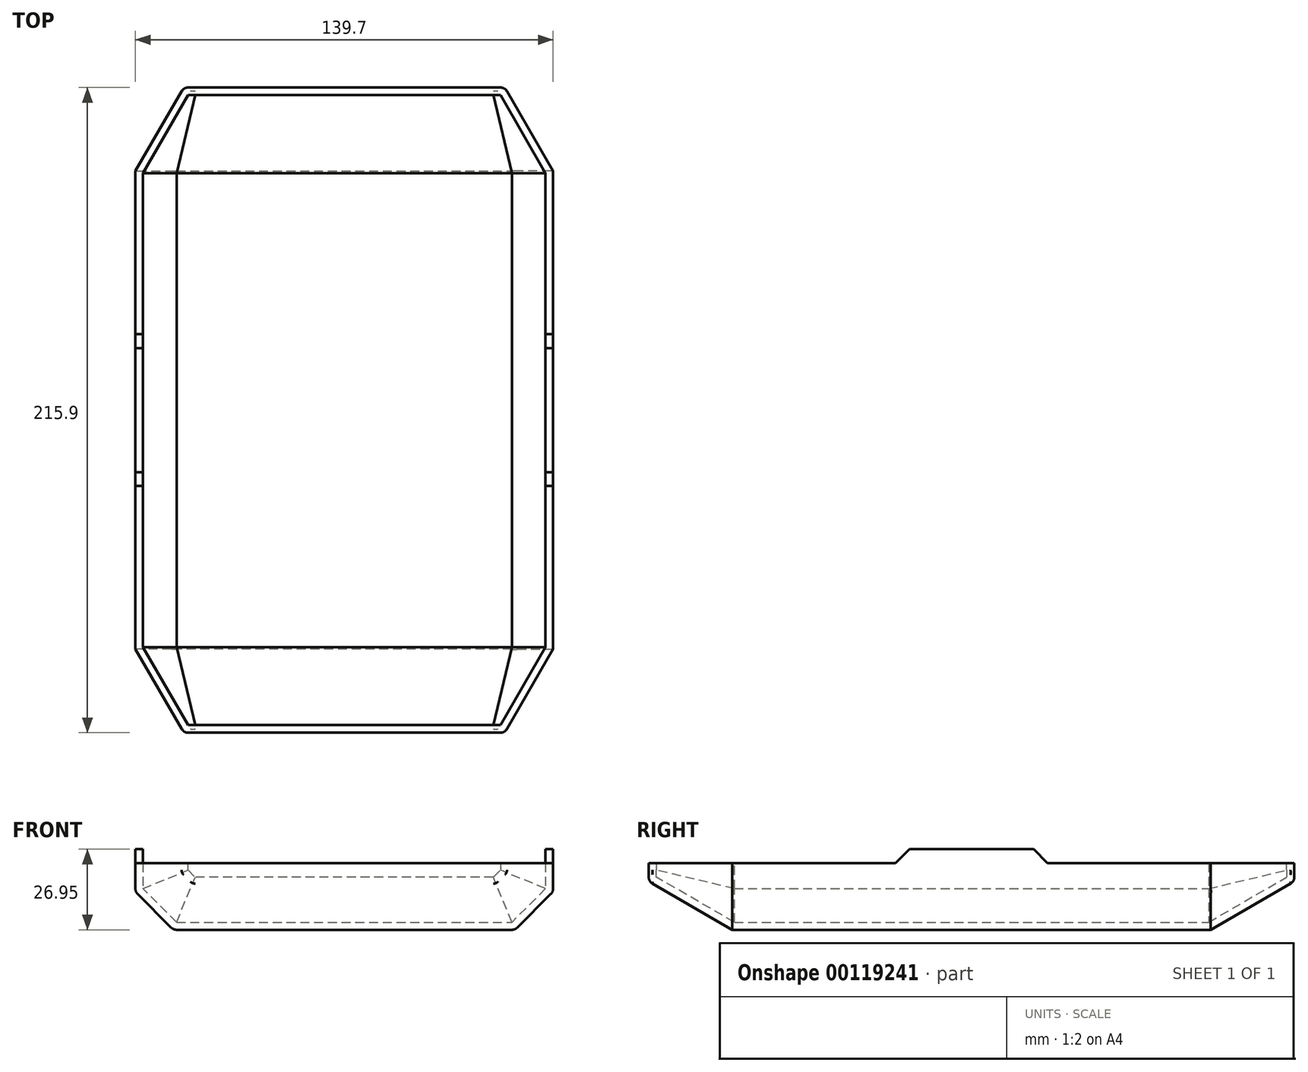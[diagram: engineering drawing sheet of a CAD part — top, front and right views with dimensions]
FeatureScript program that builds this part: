
annotation { "Feature Type Name" : "Feature", "Feature Type Description" : "" }
export const myFeature = defineFeature(function(context is Context, id is Id, definition is map)
    precondition{}
    {
        {
            var Q0;
            Q0=qCreatedBy(makeId("Right.planeOp"),FACE);
            var sketch = newSketch(context, id + "F0", { "sketchPlane" : qUnion([Q0])});
            skLineSegment(sketch, "E0", {"start": v(0, 0) * mm, "end": v(-215.9, 0) * mm});
            skLineSegment(sketch, "E1", {"start": v(-215.9, 0) * mm, "end": v(-215.9, 139.7) * mm});
            skLineSegment(sketch, "E2", {"start": v(-215.9, 139.7) * mm, "end": v(0, 139.7) * mm});
            skLineSegment(sketch, "E3", {"start": v(0, 139.7) * mm, "end": v(0, 0) * mm});
            skSolve(sketch);
        }
        {
            var Q0;
            Q0=makeQuery(id+"F0.imprint","IMPRINT",FACE,{"disambiguationData":[TD([[makeQuery(id+"F0.imprint","IMPRINT",EDGE,{"derivedFrom":sQuery(id+"F0.wireOp",EDGE,"E0")}),-1.0]])]});
            extrude(context, id + "F1", {"entities" : qUnion([Q0]), "depth" : 139.7 * mm});
        }
        {
            var Q0;
            Q0=makeQuery(id+"F1.opExtrude","CAP_EDGE",EDGE,{"disambiguationData":[OSD([sQuery(id+"F0.wireOp",EDGE,"E2")])],"isStart":true});
            var Q1;
            Q1=makeQuery(id+"F1.opExtrude","CAP_EDGE",EDGE,{"disambiguationData":[OSD([sQuery(id+"F0.wireOp",EDGE,"E0")])],"isStart":true});
            var Q2;
            Q2=makeQuery(id+"F1.opExtrude","CAP_EDGE",EDGE,{"disambiguationData":[OSD([sQuery(id+"F0.wireOp",EDGE,"E2")])],"isStart":false});
            var Q3;
            Q3=makeQuery(id+"F1.opExtrude","CAP_EDGE",EDGE,{"disambiguationData":[OSD([sQuery(id+"F0.wireOp",EDGE,"E0")])],"isStart":false});
            chamfer(context, id + "F2", {"entities" : qUnion([Q0, Q1, Q2, Q3]), "chamferType" : ChamferType.OFFSET_ANGLE, "width" : 12.7 * mm, "oppositeDirection" : false, "angle" : 45 * degree, "tangentPropagation" : true});
        }
        {
            var Q0;
            Q0=makeQuery(id+"F2.opChamfer","BLEND_EDGE",EDGE,{"blendedFrom":[makeQuery(id+"F1.opExtrude","CAP_EDGE",EDGE,{"disambiguationData":[OSD([sQuery(id+"F0.wireOp",EDGE,"E0")])],"isStart":true}),makeQuery(id+"F1.opExtrude","SWEPT_FACE",FACE,{"disambiguationData":[OSD([sQuery(id+"F0.wireOp",EDGE,"E1")])]})],"blendedInto":[makeQuery(id+"F1.opExtrude","SWEPT_FACE",FACE,{"disambiguationData":[OSD([sQuery(id+"F0.wireOp",EDGE,"E1")])]})]});
            var Q1;
            Q1=makeQuery(id+"F1.opExtrude","CAP_EDGE",EDGE,{"disambiguationData":[OSD([sQuery(id+"F0.wireOp",EDGE,"E1")])],"isStart":true});
            var Q2;
            Q2=makeQuery(id+"F2.opChamfer","BLEND_EDGE",EDGE,{"blendedFrom":[makeQuery(id+"F1.opExtrude","CAP_EDGE",EDGE,{"disambiguationData":[OSD([sQuery(id+"F0.wireOp",EDGE,"E2")])],"isStart":true}),makeQuery(id+"F1.opExtrude","SWEPT_FACE",FACE,{"disambiguationData":[OSD([sQuery(id+"F0.wireOp",EDGE,"E1")])]})],"blendedInto":[makeQuery(id+"F1.opExtrude","SWEPT_FACE",FACE,{"disambiguationData":[OSD([sQuery(id+"F0.wireOp",EDGE,"E1")])]})]});
            var Q3;
            Q3=makeQuery(id+"F1.opExtrude","SWEPT_EDGE",EDGE,{"disambiguationData":[OSD([sQuery(id+"F0.wireOp",EDGE,"E1"),sQuery(id+"F0.wireOp",EDGE,"E2")])]});
            var Q4;
            Q4=makeQuery(id+"F1.opExtrude","SWEPT_FACE",FACE,{"disambiguationData":[OSD([sQuery(id+"F0.wireOp",EDGE,"E1")])]});
            chamfer(context, id + "F3", {"entities" : qUnion([Q0, Q1, Q2, Q3, Q4]), "chamferType" : ChamferType.OFFSET_ANGLE, "width" : 27.94 * mm, "oppositeDirection" : true, "angle" : 30 * degree, "tangentPropagation" : true});
        }
        {
            var Q0;
            Q0=makeQuery(id+"F1.opExtrude","CAP_EDGE",EDGE,{"disambiguationData":[OSD([sQuery(id+"F0.wireOp",EDGE,"E3")])],"isStart":true});
            var Q1;
            Q1=makeQuery(id+"F1.opExtrude","SWEPT_EDGE",EDGE,{"disambiguationData":[OSD([sQuery(id+"F0.wireOp",EDGE,"E0"),sQuery(id+"F0.wireOp",EDGE,"E3")])]});
            var Q2;
            Q2=makeQuery(id+"F1.opExtrude","CAP_EDGE",EDGE,{"disambiguationData":[OSD([sQuery(id+"F0.wireOp",EDGE,"E3")])],"isStart":false});
            var Q3;
            Q3=makeQuery(id+"F1.opExtrude","SWEPT_EDGE",EDGE,{"disambiguationData":[OSD([sQuery(id+"F0.wireOp",EDGE,"E2"),sQuery(id+"F0.wireOp",EDGE,"E3")])]});
            var Q4;
            Q4=makeQuery(id+"F2.opChamfer","BLEND_EDGE",EDGE,{"blendedFrom":[makeQuery(id+"F1.opExtrude","CAP_EDGE",EDGE,{"disambiguationData":[OSD([sQuery(id+"F0.wireOp",EDGE,"E0")])],"isStart":false}),makeQuery(id+"F1.opExtrude","SWEPT_FACE",FACE,{"disambiguationData":[OSD([sQuery(id+"F0.wireOp",EDGE,"E3")])]})],"blendedInto":[makeQuery(id+"F1.opExtrude","SWEPT_FACE",FACE,{"disambiguationData":[OSD([sQuery(id+"F0.wireOp",EDGE,"E3")])]})]});
            var Q5;
            Q5=makeQuery(id+"F2.opChamfer","BLEND_EDGE",EDGE,{"blendedFrom":[makeQuery(id+"F1.opExtrude","CAP_EDGE",EDGE,{"disambiguationData":[OSD([sQuery(id+"F0.wireOp",EDGE,"E2")])],"isStart":false}),makeQuery(id+"F1.opExtrude","SWEPT_FACE",FACE,{"disambiguationData":[OSD([sQuery(id+"F0.wireOp",EDGE,"E3")])]})],"blendedInto":[makeQuery(id+"F1.opExtrude","SWEPT_FACE",FACE,{"disambiguationData":[OSD([sQuery(id+"F0.wireOp",EDGE,"E3")])]})]});
            var Q6;
            Q6=makeQuery(id+"F2.opChamfer","BLEND_EDGE",EDGE,{"blendedFrom":[makeQuery(id+"F1.opExtrude","CAP_EDGE",EDGE,{"disambiguationData":[OSD([sQuery(id+"F0.wireOp",EDGE,"E2")])],"isStart":true}),makeQuery(id+"F1.opExtrude","SWEPT_FACE",FACE,{"disambiguationData":[OSD([sQuery(id+"F0.wireOp",EDGE,"E3")])]})],"blendedInto":[makeQuery(id+"F1.opExtrude","SWEPT_FACE",FACE,{"disambiguationData":[OSD([sQuery(id+"F0.wireOp",EDGE,"E3")])]})]});
            var Q7;
            Q7=makeQuery(id+"F2.opChamfer","BLEND_EDGE",EDGE,{"blendedFrom":[makeQuery(id+"F1.opExtrude","CAP_EDGE",EDGE,{"disambiguationData":[OSD([sQuery(id+"F0.wireOp",EDGE,"E0")])],"isStart":true}),makeQuery(id+"F1.opExtrude","SWEPT_FACE",FACE,{"disambiguationData":[OSD([sQuery(id+"F0.wireOp",EDGE,"E3")])]})],"blendedInto":[makeQuery(id+"F1.opExtrude","SWEPT_FACE",FACE,{"disambiguationData":[OSD([sQuery(id+"F0.wireOp",EDGE,"E3")])]})]});
            chamfer(context, id + "F4", {"entities" : qUnion([Q0, Q1, Q2, Q3, Q4, Q5, Q6, Q7]), "chamferType" : ChamferType.OFFSET_ANGLE, "width" : 27.94 * mm, "oppositeDirection" : false, "angle" : 30 * degree, "tangentPropagation" : true});
        }
        {
            var Q0;
            Q0=makeQuery(id+"F1.opExtrude","SWEPT_FACE",FACE,{"disambiguationData":[OSD([sQuery(id+"F0.wireOp",EDGE,"E2")])]});
            var sketch = newSketch(context, id + "F5", { "sketchPlane" : qUnion([Q0])});
            skCircle(sketch, "E4", {"center": v(69.85, -107.95) * mm, "radius": 38.1 * mm});
            skSolve(sketch);
        }
        {
            var Q0;
            Q0=makeQuery(id+"F5.imprint","IMPRINT",FACE,{"disambiguationData":[TD([[makeQuery(id+"F5.imprint","IMPRINT",EDGE,{"derivedFrom":sQuery(id+"F5.wireOp",EDGE,"E4")}),1.0]])]});
            extrude(context, id + "F6", {"entities" : qUnion([Q0]), "operationType" : NewBodyOperationType.ADD, "depth" : 6.35 * mm});
        }
        {
            var Q0;
            {var subQ0=sQuery(id+"F0.wireOp",EDGE,"E1");Q0=makeQuery(id+"F3.opChamfer","BLEND_EDGE",EDGE,{"blendedFrom":[makeQuery(id+"F1.opExtrude","CAP_EDGE",EDGE,{"disambiguationData":[OSD([subQ0])],"isStart":false}),makeQuery(id+"F2.opChamfer","BLEND_EDGE",EDGE,{"blendedFrom":[makeQuery(id+"F1.opExtrude","CAP_EDGE",EDGE,{"disambiguationData":[OSD([sQuery(id+"F0.wireOp",EDGE,"E2")])],"isStart":false}),makeQuery(id+"F1.opExtrude","SWEPT_FACE",FACE,{"disambiguationData":[OSD([subQ0])]})],"blendedInto":[makeQuery(id+"F1.opExtrude","SWEPT_FACE",FACE,{"disambiguationData":[OSD([subQ0])]})]})],"blendedInto":[]});}
            var Q1;
            {var subQ0=sQuery(id+"F0.wireOp",EDGE,"E1");var subQ1=sQuery(id+"F0.wireOp",EDGE,"E2");Q1=makeQuery(id+"F3.opChamfer","BLEND_EDGE",EDGE,{"blendedFrom":[makeQuery(id+"F1.opExtrude","SWEPT_EDGE",EDGE,{"disambiguationData":[OSD([subQ0,subQ1])]}),makeQuery(id+"F2.opChamfer","BLEND_EDGE",EDGE,{"blendedFrom":[makeQuery(id+"F1.opExtrude","CAP_EDGE",EDGE,{"disambiguationData":[OSD([subQ1])],"isStart":false}),makeQuery(id+"F1.opExtrude","SWEPT_FACE",FACE,{"disambiguationData":[OSD([subQ0])]})],"blendedInto":[makeQuery(id+"F1.opExtrude","SWEPT_FACE",FACE,{"disambiguationData":[OSD([subQ0])]})]})],"blendedInto":[]});}
            var Q2;
            {var subQ0=sQuery(id+"F0.wireOp",EDGE,"E2");Q2=makeQuery(id+"F2.opChamfer","BLEND_EDGE",EDGE,{"blendedFrom":[makeQuery(id+"F1.opExtrude","CAP_EDGE",EDGE,{"disambiguationData":[OSD([subQ0])],"isStart":false}),makeQuery(id+"F1.opExtrude","SWEPT_FACE",FACE,{"disambiguationData":[OSD([subQ0])]})],"blendedInto":[makeQuery(id+"F1.opExtrude","SWEPT_FACE",FACE,{"disambiguationData":[OSD([subQ0])]})]});}
            var Q3;
            {var subQ0=sQuery(id+"F0.wireOp",EDGE,"E2");Q3=makeQuery(id+"F2.opChamfer","BLEND_EDGE",EDGE,{"blendedFrom":[makeQuery(id+"F1.opExtrude","CAP_EDGE",EDGE,{"disambiguationData":[OSD([subQ0])],"isStart":false}),makeQuery(id+"F1.opExtrude","CAP_FACE",FACE,{"disambiguationData":[OSD([sQuery(id+"F0.wireOp",EDGE,"E0"),sQuery(id+"F0.wireOp",EDGE,"E1"),subQ0,sQuery(id+"F0.wireOp",EDGE,"E3")])],"isStart":false})],"blendedInto":[makeQuery(id+"F1.opExtrude","CAP_FACE",FACE,{"disambiguationData":[OSD([sQuery(id+"F0.wireOp",EDGE,"E0"),sQuery(id+"F0.wireOp",EDGE,"E1"),subQ0,sQuery(id+"F0.wireOp",EDGE,"E3")])],"isStart":false})]});}
            var Q4;
            {var subQ0=makeQuery(id+"F1.opExtrude","SWEPT_FACE",FACE,{"disambiguationData":[OSD([sQuery(id+"F0.wireOp",EDGE,"E1")])]});Q4=makeQuery(id+"F3.opChamfer","BLEND_EDGE",EDGE,{"blendedFrom":[makeQuery(id+"F2.opChamfer","BLEND_EDGE",EDGE,{"blendedFrom":[makeQuery(id+"F1.opExtrude","CAP_EDGE",EDGE,{"disambiguationData":[OSD([sQuery(id+"F0.wireOp",EDGE,"E2")])],"isStart":false}),subQ0],"blendedInto":[subQ0]}),subQ0],"blendedInto":[subQ0]});}
            var Q5;
            {var subQ0=sQuery(id+"F0.wireOp",EDGE,"E1");Q5=makeQuery(id+"F3.opChamfer","BLEND_EDGE",EDGE,{"blendedFrom":[makeQuery(id+"F1.opExtrude","SWEPT_EDGE",EDGE,{"disambiguationData":[OSD([subQ0,sQuery(id+"F0.wireOp",EDGE,"E2")])]}),makeQuery(id+"F1.opExtrude","SWEPT_FACE",FACE,{"disambiguationData":[OSD([subQ0])]})],"blendedInto":[makeQuery(id+"F1.opExtrude","SWEPT_FACE",FACE,{"disambiguationData":[OSD([subQ0])]})]});}
            var Q6;
            {var subQ0=sQuery(id+"F0.wireOp",EDGE,"E1");Q6=makeQuery(id+"F3.opChamfer","BLEND_EDGE",EDGE,{"blendedFrom":[makeQuery(id+"F1.opExtrude","CAP_EDGE",EDGE,{"disambiguationData":[OSD([subQ0])],"isStart":false}),makeQuery(id+"F1.opExtrude","SWEPT_FACE",FACE,{"disambiguationData":[OSD([subQ0])]})],"blendedInto":[makeQuery(id+"F1.opExtrude","SWEPT_FACE",FACE,{"disambiguationData":[OSD([subQ0])]})]});}
            var Q7;
            {var subQ0=sQuery(id+"F0.wireOp",EDGE,"E3");var subQ1=sQuery(id+"F0.wireOp",EDGE,"E2");Q7=makeQuery(id+"F4.opChamfer","BLEND_EDGE",EDGE,{"blendedFrom":[makeQuery(id+"F1.opExtrude","SWEPT_EDGE",EDGE,{"disambiguationData":[OSD([subQ1,subQ0])]}),makeQuery(id+"F2.opChamfer","BLEND_EDGE",EDGE,{"blendedFrom":[makeQuery(id+"F1.opExtrude","CAP_EDGE",EDGE,{"disambiguationData":[OSD([subQ1])],"isStart":false}),makeQuery(id+"F1.opExtrude","SWEPT_FACE",FACE,{"disambiguationData":[OSD([subQ0])]})],"blendedInto":[makeQuery(id+"F1.opExtrude","SWEPT_FACE",FACE,{"disambiguationData":[OSD([subQ0])]})]})],"blendedInto":[]});}
            var Q8;
            {var subQ0=sQuery(id+"F0.wireOp",EDGE,"E3");Q8=makeQuery(id+"F4.opChamfer","BLEND_EDGE",EDGE,{"blendedFrom":[makeQuery(id+"F2.opChamfer","BLEND_EDGE",EDGE,{"blendedFrom":[makeQuery(id+"F1.opExtrude","CAP_EDGE",EDGE,{"disambiguationData":[OSD([sQuery(id+"F0.wireOp",EDGE,"E2")])],"isStart":false}),makeQuery(id+"F1.opExtrude","SWEPT_FACE",FACE,{"disambiguationData":[OSD([subQ0])]})],"blendedInto":[makeQuery(id+"F1.opExtrude","SWEPT_FACE",FACE,{"disambiguationData":[OSD([subQ0])]})]}),makeQuery(id+"F1.opExtrude","CAP_EDGE",EDGE,{"disambiguationData":[OSD([subQ0])],"isStart":false})],"blendedInto":[]});}
            var Q9;
            {var subQ0=makeQuery(id+"F1.opExtrude","SWEPT_FACE",FACE,{"disambiguationData":[OSD([sQuery(id+"F0.wireOp",EDGE,"E3")])]});Q9=makeQuery(id+"F4.opChamfer","BLEND_EDGE",EDGE,{"blendedFrom":[makeQuery(id+"F2.opChamfer","BLEND_EDGE",EDGE,{"blendedFrom":[makeQuery(id+"F1.opExtrude","CAP_EDGE",EDGE,{"disambiguationData":[OSD([sQuery(id+"F0.wireOp",EDGE,"E2")])],"isStart":false}),subQ0],"blendedInto":[subQ0]}),subQ0],"blendedInto":[subQ0]});}
            var Q10;
            {var subQ0=sQuery(id+"F0.wireOp",EDGE,"E3");Q10=makeQuery(id+"F4.opChamfer","BLEND_EDGE",EDGE,{"blendedFrom":[makeQuery(id+"F1.opExtrude","CAP_EDGE",EDGE,{"disambiguationData":[OSD([subQ0])],"isStart":false}),makeQuery(id+"F1.opExtrude","SWEPT_FACE",FACE,{"disambiguationData":[OSD([subQ0])]})],"blendedInto":[makeQuery(id+"F1.opExtrude","SWEPT_FACE",FACE,{"disambiguationData":[OSD([subQ0])]})]});}
            var Q11;
            {var subQ0=sQuery(id+"F0.wireOp",EDGE,"E1");Q11=makeQuery(id+"F3.opChamfer","BLEND_EDGE",EDGE,{"blendedFrom":[makeQuery(id+"F2.opChamfer","BLEND_EDGE",EDGE,{"blendedFrom":[makeQuery(id+"F1.opExtrude","CAP_EDGE",EDGE,{"disambiguationData":[OSD([sQuery(id+"F0.wireOp",EDGE,"E0")])],"isStart":false}),makeQuery(id+"F1.opExtrude","SWEPT_FACE",FACE,{"disambiguationData":[OSD([subQ0])]})],"blendedInto":[makeQuery(id+"F1.opExtrude","SWEPT_FACE",FACE,{"disambiguationData":[OSD([subQ0])]})]}),makeQuery(id+"F1.opExtrude","CAP_EDGE",EDGE,{"disambiguationData":[OSD([subQ0])],"isStart":false})],"blendedInto":[]});}
            var Q12;
            {var subQ0=sQuery(id+"F0.wireOp",EDGE,"E1");var subQ1=sQuery(id+"F0.wireOp",EDGE,"E0");Q12=makeQuery(id+"F3.opChamfer","BLEND_EDGE",EDGE,{"blendedFrom":[makeQuery(id+"F1.opExtrude","SWEPT_EDGE",EDGE,{"disambiguationData":[OSD([subQ1,subQ0])]}),makeQuery(id+"F2.opChamfer","BLEND_EDGE",EDGE,{"blendedFrom":[makeQuery(id+"F1.opExtrude","CAP_EDGE",EDGE,{"disambiguationData":[OSD([subQ1])],"isStart":false}),makeQuery(id+"F1.opExtrude","SWEPT_FACE",FACE,{"disambiguationData":[OSD([subQ0])]})],"blendedInto":[makeQuery(id+"F1.opExtrude","SWEPT_FACE",FACE,{"disambiguationData":[OSD([subQ0])]})]})],"blendedInto":[]});}
            var Q13;
            {var subQ0=makeQuery(id+"F1.opExtrude","SWEPT_FACE",FACE,{"disambiguationData":[OSD([sQuery(id+"F0.wireOp",EDGE,"E1")])]});Q13=makeQuery(id+"F3.opChamfer","BLEND_EDGE",EDGE,{"blendedFrom":[makeQuery(id+"F2.opChamfer","BLEND_EDGE",EDGE,{"blendedFrom":[makeQuery(id+"F1.opExtrude","CAP_EDGE",EDGE,{"disambiguationData":[OSD([sQuery(id+"F0.wireOp",EDGE,"E0")])],"isStart":false}),subQ0],"blendedInto":[subQ0]}),subQ0],"blendedInto":[subQ0]});}
            var Q14;
            {var subQ0=sQuery(id+"F0.wireOp",EDGE,"E1");Q14=makeQuery(id+"F3.opChamfer","BLEND_EDGE",EDGE,{"blendedFrom":[makeQuery(id+"F1.opExtrude","SWEPT_EDGE",EDGE,{"disambiguationData":[OSD([sQuery(id+"F0.wireOp",EDGE,"E0"),subQ0])]}),makeQuery(id+"F1.opExtrude","SWEPT_FACE",FACE,{"disambiguationData":[OSD([subQ0])]})],"blendedInto":[makeQuery(id+"F1.opExtrude","SWEPT_FACE",FACE,{"disambiguationData":[OSD([subQ0])]})]});}
            var Q15;
            {var subQ0=sQuery(id+"F0.wireOp",EDGE,"E1");var subQ1=sQuery(id+"F0.wireOp",EDGE,"E0");Q15=makeQuery(id+"F3.opChamfer","BLEND_EDGE",EDGE,{"blendedFrom":[makeQuery(id+"F1.opExtrude","SWEPT_EDGE",EDGE,{"disambiguationData":[OSD([subQ1,subQ0])]}),makeQuery(id+"F2.opChamfer","BLEND_EDGE",EDGE,{"blendedFrom":[makeQuery(id+"F1.opExtrude","CAP_EDGE",EDGE,{"disambiguationData":[OSD([subQ1])],"isStart":true}),makeQuery(id+"F1.opExtrude","SWEPT_FACE",FACE,{"disambiguationData":[OSD([subQ0])]})],"blendedInto":[makeQuery(id+"F1.opExtrude","SWEPT_FACE",FACE,{"disambiguationData":[OSD([subQ0])]})]})],"blendedInto":[]});}
            var Q16;
            {var subQ0=sQuery(id+"F0.wireOp",EDGE,"E1");Q16=makeQuery(id+"F3.opChamfer","BLEND_EDGE",EDGE,{"blendedFrom":[makeQuery(id+"F1.opExtrude","CAP_EDGE",EDGE,{"disambiguationData":[OSD([subQ0])],"isStart":true}),makeQuery(id+"F1.opExtrude","SWEPT_FACE",FACE,{"disambiguationData":[OSD([subQ0])]})],"blendedInto":[makeQuery(id+"F1.opExtrude","SWEPT_FACE",FACE,{"disambiguationData":[OSD([subQ0])]})]});}
            var Q17;
            {var subQ0=makeQuery(id+"F1.opExtrude","SWEPT_FACE",FACE,{"disambiguationData":[OSD([sQuery(id+"F0.wireOp",EDGE,"E1")])]});Q17=makeQuery(id+"F3.opChamfer","BLEND_EDGE",EDGE,{"blendedFrom":[makeQuery(id+"F2.opChamfer","BLEND_EDGE",EDGE,{"blendedFrom":[makeQuery(id+"F1.opExtrude","CAP_EDGE",EDGE,{"disambiguationData":[OSD([sQuery(id+"F0.wireOp",EDGE,"E0")])],"isStart":true}),subQ0],"blendedInto":[subQ0]}),subQ0],"blendedInto":[subQ0]});}
            var Q18;
            {var subQ0=makeQuery(id+"F1.opExtrude","SWEPT_FACE",FACE,{"disambiguationData":[OSD([sQuery(id+"F0.wireOp",EDGE,"E1")])]});Q18=makeQuery(id+"F3.opChamfer","BLEND_EDGE",EDGE,{"blendedFrom":[makeQuery(id+"F2.opChamfer","BLEND_EDGE",EDGE,{"blendedFrom":[makeQuery(id+"F1.opExtrude","CAP_EDGE",EDGE,{"disambiguationData":[OSD([sQuery(id+"F0.wireOp",EDGE,"E2")])],"isStart":true}),subQ0],"blendedInto":[subQ0]}),subQ0],"blendedInto":[subQ0]});}
            var Q19;
            {var subQ0=sQuery(id+"F0.wireOp",EDGE,"E1");var subQ1=sQuery(id+"F0.wireOp",EDGE,"E2");Q19=makeQuery(id+"F3.opChamfer","BLEND_EDGE",EDGE,{"blendedFrom":[makeQuery(id+"F1.opExtrude","SWEPT_EDGE",EDGE,{"disambiguationData":[OSD([subQ0,subQ1])]}),makeQuery(id+"F2.opChamfer","BLEND_EDGE",EDGE,{"blendedFrom":[makeQuery(id+"F1.opExtrude","CAP_EDGE",EDGE,{"disambiguationData":[OSD([subQ1])],"isStart":true}),makeQuery(id+"F1.opExtrude","SWEPT_FACE",FACE,{"disambiguationData":[OSD([subQ0])]})],"blendedInto":[makeQuery(id+"F1.opExtrude","SWEPT_FACE",FACE,{"disambiguationData":[OSD([subQ0])]})]})],"blendedInto":[]});}
            var Q20;
            {var subQ0=sQuery(id+"F0.wireOp",EDGE,"E1");Q20=makeQuery(id+"F3.opChamfer","BLEND_EDGE",EDGE,{"blendedFrom":[makeQuery(id+"F1.opExtrude","CAP_EDGE",EDGE,{"disambiguationData":[OSD([subQ0])],"isStart":true}),makeQuery(id+"F2.opChamfer","BLEND_EDGE",EDGE,{"blendedFrom":[makeQuery(id+"F1.opExtrude","CAP_EDGE",EDGE,{"disambiguationData":[OSD([sQuery(id+"F0.wireOp",EDGE,"E2")])],"isStart":true}),makeQuery(id+"F1.opExtrude","SWEPT_FACE",FACE,{"disambiguationData":[OSD([subQ0])]})],"blendedInto":[makeQuery(id+"F1.opExtrude","SWEPT_FACE",FACE,{"disambiguationData":[OSD([subQ0])]})]})],"blendedInto":[]});}
            var Q21;
            {var subQ0=sQuery(id+"F0.wireOp",EDGE,"E1");Q21=makeQuery(id+"F3.opChamfer","BLEND_EDGE",EDGE,{"blendedFrom":[makeQuery(id+"F2.opChamfer","BLEND_EDGE",EDGE,{"blendedFrom":[makeQuery(id+"F1.opExtrude","CAP_EDGE",EDGE,{"disambiguationData":[OSD([sQuery(id+"F0.wireOp",EDGE,"E0")])],"isStart":true}),makeQuery(id+"F1.opExtrude","SWEPT_FACE",FACE,{"disambiguationData":[OSD([subQ0])]})],"blendedInto":[makeQuery(id+"F1.opExtrude","SWEPT_FACE",FACE,{"disambiguationData":[OSD([subQ0])]})]}),makeQuery(id+"F1.opExtrude","CAP_EDGE",EDGE,{"disambiguationData":[OSD([subQ0])],"isStart":true})],"blendedInto":[]});}
            var Q22;
            {var subQ0=sQuery(id+"F0.wireOp",EDGE,"E0");Q22=makeQuery(id+"F2.opChamfer","BLEND_EDGE",EDGE,{"blendedFrom":[makeQuery(id+"F1.opExtrude","CAP_EDGE",EDGE,{"disambiguationData":[OSD([subQ0])],"isStart":true}),makeQuery(id+"F1.opExtrude","CAP_FACE",FACE,{"disambiguationData":[OSD([subQ0,sQuery(id+"F0.wireOp",EDGE,"E1"),sQuery(id+"F0.wireOp",EDGE,"E2"),sQuery(id+"F0.wireOp",EDGE,"E3")])],"isStart":true})],"blendedInto":[makeQuery(id+"F1.opExtrude","CAP_FACE",FACE,{"disambiguationData":[OSD([subQ0,sQuery(id+"F0.wireOp",EDGE,"E1"),sQuery(id+"F0.wireOp",EDGE,"E2"),sQuery(id+"F0.wireOp",EDGE,"E3")])],"isStart":true})]});}
            var Q23;
            {var subQ0=sQuery(id+"F0.wireOp",EDGE,"E2");Q23=makeQuery(id+"F2.opChamfer","BLEND_EDGE",EDGE,{"blendedFrom":[makeQuery(id+"F1.opExtrude","CAP_EDGE",EDGE,{"disambiguationData":[OSD([subQ0])],"isStart":true}),makeQuery(id+"F1.opExtrude","SWEPT_FACE",FACE,{"disambiguationData":[OSD([subQ0])]})],"blendedInto":[makeQuery(id+"F1.opExtrude","SWEPT_FACE",FACE,{"disambiguationData":[OSD([subQ0])]})]});}
            var Q24;
            {var subQ0=sQuery(id+"F0.wireOp",EDGE,"E2");Q24=makeQuery(id+"F2.opChamfer","BLEND_EDGE",EDGE,{"blendedFrom":[makeQuery(id+"F1.opExtrude","CAP_EDGE",EDGE,{"disambiguationData":[OSD([subQ0])],"isStart":true}),makeQuery(id+"F1.opExtrude","CAP_FACE",FACE,{"disambiguationData":[OSD([sQuery(id+"F0.wireOp",EDGE,"E0"),sQuery(id+"F0.wireOp",EDGE,"E1"),subQ0,sQuery(id+"F0.wireOp",EDGE,"E3")])],"isStart":true})],"blendedInto":[makeQuery(id+"F1.opExtrude","CAP_FACE",FACE,{"disambiguationData":[OSD([sQuery(id+"F0.wireOp",EDGE,"E0"),sQuery(id+"F0.wireOp",EDGE,"E1"),subQ0,sQuery(id+"F0.wireOp",EDGE,"E3")])],"isStart":true})]});}
            var Q25;
            {var subQ0=sQuery(id+"F0.wireOp",EDGE,"E3");var subQ1=sQuery(id+"F0.wireOp",EDGE,"E2");Q25=makeQuery(id+"F4.opChamfer","BLEND_EDGE",EDGE,{"blendedFrom":[makeQuery(id+"F1.opExtrude","SWEPT_EDGE",EDGE,{"disambiguationData":[OSD([subQ1,subQ0])]}),makeQuery(id+"F2.opChamfer","BLEND_EDGE",EDGE,{"blendedFrom":[makeQuery(id+"F1.opExtrude","CAP_EDGE",EDGE,{"disambiguationData":[OSD([subQ1])],"isStart":true}),makeQuery(id+"F1.opExtrude","SWEPT_FACE",FACE,{"disambiguationData":[OSD([subQ0])]})],"blendedInto":[makeQuery(id+"F1.opExtrude","SWEPT_FACE",FACE,{"disambiguationData":[OSD([subQ0])]})]})],"blendedInto":[]});}
            var Q26;
            {var subQ0=sQuery(id+"F0.wireOp",EDGE,"E3");Q26=makeQuery(id+"F4.opChamfer","BLEND_EDGE",EDGE,{"blendedFrom":[makeQuery(id+"F2.opChamfer","BLEND_EDGE",EDGE,{"blendedFrom":[makeQuery(id+"F1.opExtrude","CAP_EDGE",EDGE,{"disambiguationData":[OSD([sQuery(id+"F0.wireOp",EDGE,"E2")])],"isStart":true}),makeQuery(id+"F1.opExtrude","SWEPT_FACE",FACE,{"disambiguationData":[OSD([subQ0])]})],"blendedInto":[makeQuery(id+"F1.opExtrude","SWEPT_FACE",FACE,{"disambiguationData":[OSD([subQ0])]})]}),makeQuery(id+"F1.opExtrude","CAP_EDGE",EDGE,{"disambiguationData":[OSD([subQ0])],"isStart":true})],"blendedInto":[]});}
            var Q27;
            {var subQ0=makeQuery(id+"F1.opExtrude","SWEPT_FACE",FACE,{"disambiguationData":[OSD([sQuery(id+"F0.wireOp",EDGE,"E3")])]});Q27=makeQuery(id+"F4.opChamfer","BLEND_EDGE",EDGE,{"blendedFrom":[makeQuery(id+"F2.opChamfer","BLEND_EDGE",EDGE,{"blendedFrom":[makeQuery(id+"F1.opExtrude","CAP_EDGE",EDGE,{"disambiguationData":[OSD([sQuery(id+"F0.wireOp",EDGE,"E2")])],"isStart":true}),subQ0],"blendedInto":[subQ0]}),subQ0],"blendedInto":[subQ0]});}
            var Q28;
            {var subQ0=sQuery(id+"F0.wireOp",EDGE,"E3");Q28=makeQuery(id+"F4.opChamfer","BLEND_EDGE",EDGE,{"blendedFrom":[makeQuery(id+"F1.opExtrude","SWEPT_EDGE",EDGE,{"disambiguationData":[OSD([sQuery(id+"F0.wireOp",EDGE,"E2"),subQ0])]}),makeQuery(id+"F1.opExtrude","SWEPT_FACE",FACE,{"disambiguationData":[OSD([subQ0])]})],"blendedInto":[makeQuery(id+"F1.opExtrude","SWEPT_FACE",FACE,{"disambiguationData":[OSD([subQ0])]})]});}
            var Q29;
            {var subQ0=sQuery(id+"F0.wireOp",EDGE,"E3");Q29=makeQuery(id+"F4.opChamfer","BLEND_EDGE",EDGE,{"blendedFrom":[makeQuery(id+"F1.opExtrude","CAP_EDGE",EDGE,{"disambiguationData":[OSD([subQ0])],"isStart":true}),makeQuery(id+"F1.opExtrude","SWEPT_FACE",FACE,{"disambiguationData":[OSD([subQ0])]})],"blendedInto":[makeQuery(id+"F1.opExtrude","SWEPT_FACE",FACE,{"disambiguationData":[OSD([subQ0])]})]});}
            var Q30;
            {var subQ0=sQuery(id+"F0.wireOp",EDGE,"E3");Q30=makeQuery(id+"F4.opChamfer","BLEND_EDGE",EDGE,{"blendedFrom":[makeQuery(id+"F2.opChamfer","BLEND_EDGE",EDGE,{"blendedFrom":[makeQuery(id+"F1.opExtrude","CAP_EDGE",EDGE,{"disambiguationData":[OSD([sQuery(id+"F0.wireOp",EDGE,"E0")])],"isStart":true}),makeQuery(id+"F1.opExtrude","SWEPT_FACE",FACE,{"disambiguationData":[OSD([subQ0])]})],"blendedInto":[makeQuery(id+"F1.opExtrude","SWEPT_FACE",FACE,{"disambiguationData":[OSD([subQ0])]})]}),makeQuery(id+"F1.opExtrude","CAP_EDGE",EDGE,{"disambiguationData":[OSD([subQ0])],"isStart":true})],"blendedInto":[]});}
            var Q31;
            {var subQ0=sQuery(id+"F0.wireOp",EDGE,"E3");var subQ1=sQuery(id+"F0.wireOp",EDGE,"E0");Q31=makeQuery(id+"F4.opChamfer","BLEND_EDGE",EDGE,{"blendedFrom":[makeQuery(id+"F1.opExtrude","SWEPT_EDGE",EDGE,{"disambiguationData":[OSD([subQ1,subQ0])]}),makeQuery(id+"F2.opChamfer","BLEND_EDGE",EDGE,{"blendedFrom":[makeQuery(id+"F1.opExtrude","CAP_EDGE",EDGE,{"disambiguationData":[OSD([subQ1])],"isStart":true}),makeQuery(id+"F1.opExtrude","SWEPT_FACE",FACE,{"disambiguationData":[OSD([subQ0])]})],"blendedInto":[makeQuery(id+"F1.opExtrude","SWEPT_FACE",FACE,{"disambiguationData":[OSD([subQ0])]})]})],"blendedInto":[]});}
            var Q32;
            {var subQ0=makeQuery(id+"F1.opExtrude","SWEPT_FACE",FACE,{"disambiguationData":[OSD([sQuery(id+"F0.wireOp",EDGE,"E3")])]});Q32=makeQuery(id+"F4.opChamfer","BLEND_EDGE",EDGE,{"blendedFrom":[makeQuery(id+"F2.opChamfer","BLEND_EDGE",EDGE,{"blendedFrom":[makeQuery(id+"F1.opExtrude","CAP_EDGE",EDGE,{"disambiguationData":[OSD([sQuery(id+"F0.wireOp",EDGE,"E0")])],"isStart":true}),subQ0],"blendedInto":[subQ0]}),subQ0],"blendedInto":[subQ0]});}
            var Q33;
            {var subQ0=sQuery(id+"F0.wireOp",EDGE,"E3");Q33=makeQuery(id+"F4.opChamfer","BLEND_EDGE",EDGE,{"blendedFrom":[makeQuery(id+"F1.opExtrude","SWEPT_EDGE",EDGE,{"disambiguationData":[OSD([sQuery(id+"F0.wireOp",EDGE,"E0"),subQ0])]}),makeQuery(id+"F1.opExtrude","SWEPT_FACE",FACE,{"disambiguationData":[OSD([subQ0])]})],"blendedInto":[makeQuery(id+"F1.opExtrude","SWEPT_FACE",FACE,{"disambiguationData":[OSD([subQ0])]})]});}
            var Q34;
            {var subQ0=makeQuery(id+"F1.opExtrude","SWEPT_FACE",FACE,{"disambiguationData":[OSD([sQuery(id+"F0.wireOp",EDGE,"E3")])]});Q34=makeQuery(id+"F4.opChamfer","BLEND_EDGE",EDGE,{"blendedFrom":[makeQuery(id+"F2.opChamfer","BLEND_EDGE",EDGE,{"blendedFrom":[makeQuery(id+"F1.opExtrude","CAP_EDGE",EDGE,{"disambiguationData":[OSD([sQuery(id+"F0.wireOp",EDGE,"E0")])],"isStart":false}),subQ0],"blendedInto":[subQ0]}),subQ0],"blendedInto":[subQ0]});}
            var Q35;
            {var subQ0=sQuery(id+"F0.wireOp",EDGE,"E3");Q35=makeQuery(id+"F4.opChamfer","BLEND_EDGE",EDGE,{"blendedFrom":[makeQuery(id+"F2.opChamfer","BLEND_EDGE",EDGE,{"blendedFrom":[makeQuery(id+"F1.opExtrude","CAP_EDGE",EDGE,{"disambiguationData":[OSD([sQuery(id+"F0.wireOp",EDGE,"E0")])],"isStart":false}),makeQuery(id+"F1.opExtrude","SWEPT_FACE",FACE,{"disambiguationData":[OSD([subQ0])]})],"blendedInto":[makeQuery(id+"F1.opExtrude","SWEPT_FACE",FACE,{"disambiguationData":[OSD([subQ0])]})]}),makeQuery(id+"F1.opExtrude","CAP_EDGE",EDGE,{"disambiguationData":[OSD([subQ0])],"isStart":false})],"blendedInto":[]});}
            var Q36;
            {var subQ0=sQuery(id+"F0.wireOp",EDGE,"E3");var subQ1=sQuery(id+"F0.wireOp",EDGE,"E0");Q36=makeQuery(id+"F4.opChamfer","BLEND_EDGE",EDGE,{"blendedFrom":[makeQuery(id+"F1.opExtrude","SWEPT_EDGE",EDGE,{"disambiguationData":[OSD([subQ1,subQ0])]}),makeQuery(id+"F2.opChamfer","BLEND_EDGE",EDGE,{"blendedFrom":[makeQuery(id+"F1.opExtrude","CAP_EDGE",EDGE,{"disambiguationData":[OSD([subQ1])],"isStart":false}),makeQuery(id+"F1.opExtrude","SWEPT_FACE",FACE,{"disambiguationData":[OSD([subQ0])]})],"blendedInto":[makeQuery(id+"F1.opExtrude","SWEPT_FACE",FACE,{"disambiguationData":[OSD([subQ0])]})]})],"blendedInto":[]});}
            var Q37;
            {var subQ0=sQuery(id+"F0.wireOp",EDGE,"E0");Q37=makeQuery(id+"F2.opChamfer","BLEND_EDGE",EDGE,{"blendedFrom":[makeQuery(id+"F1.opExtrude","CAP_EDGE",EDGE,{"disambiguationData":[OSD([subQ0])],"isStart":false}),makeQuery(id+"F1.opExtrude","SWEPT_FACE",FACE,{"disambiguationData":[OSD([subQ0])]})],"blendedInto":[makeQuery(id+"F1.opExtrude","SWEPT_FACE",FACE,{"disambiguationData":[OSD([subQ0])]})]});}
            var Q38;
            {var subQ0=sQuery(id+"F0.wireOp",EDGE,"E0");Q38=makeQuery(id+"F2.opChamfer","BLEND_EDGE",EDGE,{"blendedFrom":[makeQuery(id+"F1.opExtrude","CAP_EDGE",EDGE,{"disambiguationData":[OSD([subQ0])],"isStart":false}),makeQuery(id+"F1.opExtrude","CAP_FACE",FACE,{"disambiguationData":[OSD([subQ0,sQuery(id+"F0.wireOp",EDGE,"E1"),sQuery(id+"F0.wireOp",EDGE,"E2"),sQuery(id+"F0.wireOp",EDGE,"E3")])],"isStart":false})],"blendedInto":[makeQuery(id+"F1.opExtrude","CAP_FACE",FACE,{"disambiguationData":[OSD([subQ0,sQuery(id+"F0.wireOp",EDGE,"E1"),sQuery(id+"F0.wireOp",EDGE,"E2"),sQuery(id+"F0.wireOp",EDGE,"E3")])],"isStart":false})]});}
            var Q39;
            {var subQ0=sQuery(id+"F0.wireOp",EDGE,"E0");Q39=makeQuery(id+"F2.opChamfer","BLEND_EDGE",EDGE,{"blendedFrom":[makeQuery(id+"F1.opExtrude","CAP_EDGE",EDGE,{"disambiguationData":[OSD([subQ0])],"isStart":true}),makeQuery(id+"F1.opExtrude","SWEPT_FACE",FACE,{"disambiguationData":[OSD([subQ0])]})],"blendedInto":[makeQuery(id+"F1.opExtrude","SWEPT_FACE",FACE,{"disambiguationData":[OSD([subQ0])]})]});}
            fillet(context, id + "F7", {"entities" : qUnion([Q0, Q1, Q2, Q3, Q4, Q5, Q6, Q7, Q8, Q9, Q10, Q11, Q12, Q13, Q14, Q15, Q16, Q17, Q18, Q19, Q20, Q21, Q22, Q23, Q24, Q25, Q26, Q27, Q28, Q29, Q30, Q31, Q32, Q33, Q34, Q35, Q36, Q37, Q38, Q39]), "radius" : 2.54 * mm, "tangentPropagation" : true, "allowEdgeOverflow" : false});
        }
        {
            var Q0;
            Q0=makeQuery(id+"F1.opExtrude","CAP_FACE",FACE,{"disambiguationData":[OSD([sQuery(id+"F0.wireOp",EDGE,"E0"),sQuery(id+"F0.wireOp",EDGE,"E1"),sQuery(id+"F0.wireOp",EDGE,"E2"),sQuery(id+"F0.wireOp",EDGE,"E3")])],"isStart":true});
            var sketch = newSketch(context, id + "F8", { "sketchPlane" : qUnion([Q0])});
            skLineSegment(sketch, "E5", {"start": v(82.55, 22.32) * mm, "end": v(87.18, 26.95) * mm});
            skLineSegment(sketch, "E6", {"start": v(128.72, 26.95) * mm, "end": v(133.35, 22.32) * mm});
            skLineSegment(sketch, "E7", {"start": v(128.72, 26.95) * mm, "end": v(87.18, 26.95) * mm});
            skLineSegment(sketch, "E8", {"start": v(133.35, 22.32) * mm, "end": v(242.37, 22.32) * mm});
            skLineSegment(sketch, "E9", {"start": v(82.55, 22.32) * mm, "end": v(-22.96, 22.32) * mm});
            skLineSegment(sketch, "E10", {"start": v(-22.96, 22.32) * mm, "end": v(-22.96, 184.72) * mm});
            skLineSegment(sketch, "E11", {"start": v(-22.96, 184.72) * mm, "end": v(257.24, 187.7) * mm});
            skLineSegment(sketch, "E12", {"start": v(257.24, 187.7) * mm, "end": v(242.37, 22.32) * mm});
            skSolve(sketch);
        }
        {
            var Q0;
            Q0=qSketchRegion(id+"F8",true);
            extrude(context, id + "F9", {"entities" : qUnion([Q0]), "operationType" : NewBodyOperationType.REMOVE, "oppositeDirection" : true, "depth" : 209.15 * mm});
        }
        {
            var Q0;
            Q0=makeQuery(id+"F9.boolean.opBoolean","COPY",FACE,{"derivedFrom":makeQuery(id+"F9.opExtrude","SWEPT_FACE",FACE,{"disambiguationData":[OSD([sQuery(id+"F8.wireOp",EDGE,"E9")])]})});
            var Q1;
            Q1=makeQuery(id+"F9.boolean.opBoolean","COPY",FACE,{"derivedFrom":makeQuery(id+"F9.opExtrude","SWEPT_FACE",FACE,{"disambiguationData":[OSD([sQuery(id+"F8.wireOp",EDGE,"E7")])]})});
            var Q2;
            Q2=makeQuery(id+"F9.boolean.opBoolean","COPY",FACE,{"derivedFrom":makeQuery(id+"F9.opExtrude","SWEPT_FACE",FACE,{"disambiguationData":[OSD([sQuery(id+"F8.wireOp",EDGE,"E8")])]})});
            var Q3;
            Q3=makeQuery(id+"F9.boolean.opBoolean","COPY",FACE,{"derivedFrom":makeQuery(id+"F9.opExtrude","SWEPT_FACE",FACE,{"disambiguationData":[OSD([sQuery(id+"F8.wireOp",EDGE,"E6")])]})});
            var Q4;
            Q4=makeQuery(id+"F9.boolean.opBoolean","COPY",FACE,{"derivedFrom":makeQuery(id+"F9.opExtrude","SWEPT_FACE",FACE,{"disambiguationData":[OSD([sQuery(id+"F8.wireOp",EDGE,"E5")])]})});
            shell(context, id + "F10", {"entities" : qUnion([Q0, Q1, Q2, Q3, Q4]), "thickness" : 2.54 * mm});
        }
    });
